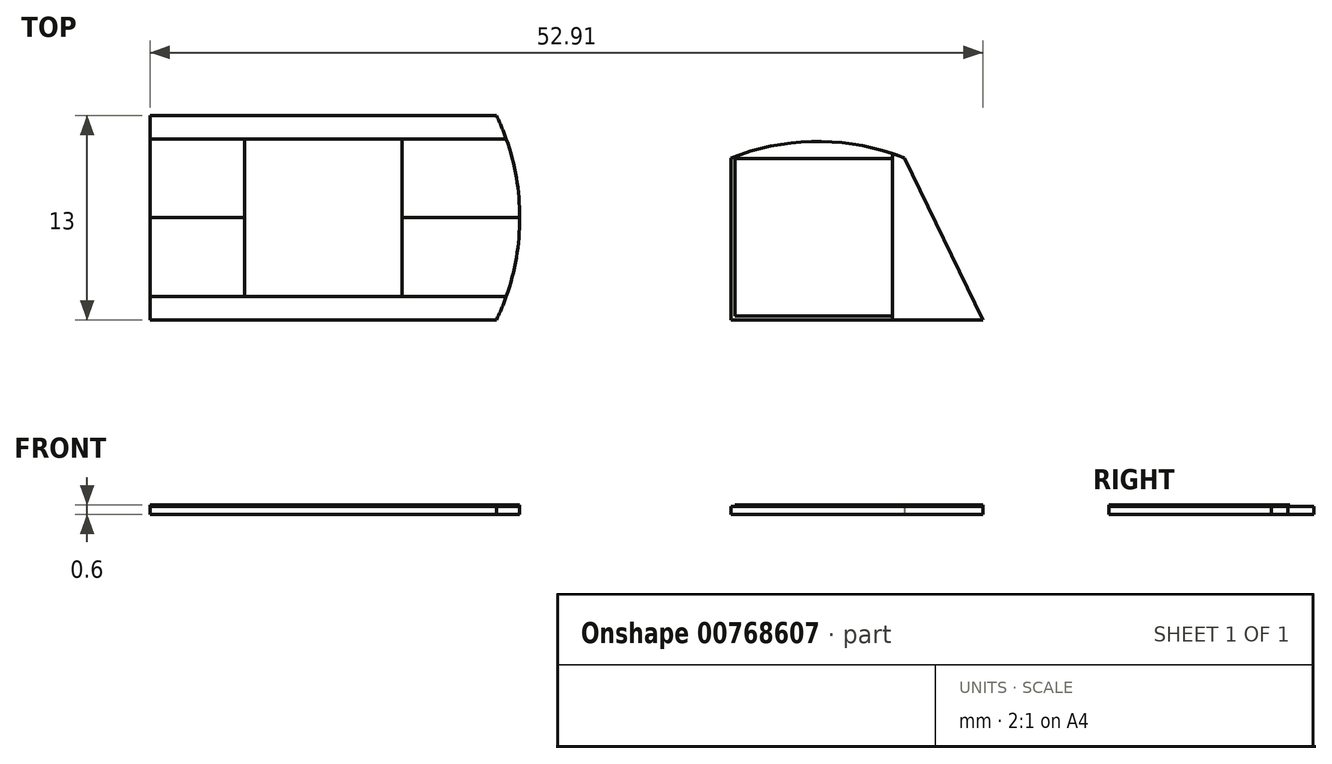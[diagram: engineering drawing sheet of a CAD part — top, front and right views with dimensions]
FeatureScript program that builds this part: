
annotation { "Feature Type Name" : "Feature", "Feature Type Description" : "" }
export const myFeature = defineFeature(function(context is Context, id is Id, definition is map)
    precondition{}
    {
        {
            var Q0;
            Q0=qCreatedBy(makeId("Top.planeOp"),FACE);
            var sketch = newSketch(context, id + "F0", { "sketchPlane" : qUnion([Q0])});
            skLineSegment(sketch, "E0.bottom", {"start": v(-26.15, 13) * mm, "end": v(-4.15, 13) * mm});
            skLineSegment(sketch, "E0.top", {"start": v(-26.15, 0) * mm, "end": v(-4.15, 0) * mm});
            skLineSegment(sketch, "E0.left", {"start": v(-26.15, 13) * mm, "end": v(-26.15, 0) * mm});
            skLineSegment(sketch, "E0.right", {"start": v(-4.15, 13) * mm, "end": v(-4.15, 0) * mm});
            skLineSegment(sketch, "E1.bottom", {"start": v(10.76, 10.3) * mm, "end": v(21.76, 10.3) * mm});
            skLineSegment(sketch, "E1.top", {"start": v(10.76, 0) * mm, "end": v(26.76, 0) * mm});
            skLineSegment(sketch, "E1.left", {"start": v(10.76, 10.3) * mm, "end": v(10.76, 0) * mm});
            skLineSegment(sketch, "E2", {"start": v(21.76, 10.3) * mm, "end": v(26.76, 0) * mm});
            skArc(sketch, "E3", {"start": v(-4.15, 0) * mm, "mid": v(-2.67, 6.5) * mm, "end": v(-4.15, 13) * mm});
            skArc(sketch, "E4", {"start": v(21.76, 10.3) * mm, "mid": v(16.26, 11.34) * mm, "end": v(10.76, 10.3) * mm});
            skSolve(sketch);
        }
        {
            var Q0;
            Q0=qSketchRegion(id+"F0",true);
            extrude(context, id + "F1", {"entities" : qUnion([Q0]), "depth" : 0.5 * mm, "offsetDistance" : 25 * mm});
        }
        {
            var Q0;
            Q0=makeQuery(id+"F1.opExtrude","CAP_FACE",FACE,{"disambiguationData":[OSD([sQuery(id+"F0.wireOp",EDGE,"E0.bottom"),sQuery(id+"F0.wireOp",EDGE,"E0.top"),sQuery(id+"F0.wireOp",EDGE,"E0.left"),sQuery(id+"F0.wireOp",EDGE,"E3")])],"isStart":false});
            var sketch = newSketch(context, id + "F2", { "sketchPlane" : qUnion([Q0])});
            skLineSegment(sketch, "E5", {"start": v(-26.15, 6.5) * mm, "end": v(-2.67, 6.5) * mm, "construction": true});
            skLineSegment(sketch, "E6.bottom", {"start": v(-10.15, 1.5) * mm, "end": v(-20.15, 1.5) * mm});
            skLineSegment(sketch, "E6.top", {"start": v(-10.15, 11.5) * mm, "end": v(-20.15, 11.5) * mm});
            skLineSegment(sketch, "E6.left", {"start": v(-10.15, 1.5) * mm, "end": v(-10.15, 11.5) * mm});
            skLineSegment(sketch, "E6.right", {"start": v(-20.15, 1.5) * mm, "end": v(-20.15, 11.5) * mm});
            skPoint(sketch, "E6.middle", {"position": v(-15.15, 6.5) * mm});
            skLineSegment(sketch, "E7.bottom", {"start": v(-20.15, 1.5) * mm, "end": v(-26.15, 1.5) * mm});
            skLineSegment(sketch, "E7.top", {"start": v(-20.15, 11.5) * mm, "end": v(-26.15, 11.5) * mm});
            skLineSegment(sketch, "E7.right", {"start": v(-26.15, 1.5) * mm, "end": v(-26.15, 11.5) * mm});
            skPoint(sketch, "E7.middle", {"position": v(-23.15, 6.5) * mm});
            skLineSegment(sketch, "E8.bottom", {"start": v(-10.15, 1.5) * mm, "end": v(-2.67, 1.5) * mm});
            skLineSegment(sketch, "E8.top", {"start": v(-10.15, 11.5) * mm, "end": v(-2.67, 11.5) * mm});
            skLineSegment(sketch, "E8.right", {"start": v(-2.67, 1.5) * mm, "end": v(-2.67, 11.5) * mm});
            skPoint(sketch, "E8.middle", {"position": v(-6.4, 6.5) * mm});
            skLineSegment(sketch, "E9", {"start": v(-20.15, 6.5) * mm, "end": v(-26.15, 6.5) * mm});
            skLineSegment(sketch, "E10", {"start": v(-10.15, 6.5) * mm, "end": v(-2.67, 6.5) * mm});
            skSolve(sketch);
        }
        {
            var Q0;
            Q0=makeQuery(id+"F1.opExtrude","CAP_FACE",FACE,{"disambiguationData":[OSD([sQuery(id+"F0.wireOp",EDGE,"E1.top"),sQuery(id+"F0.wireOp",EDGE,"E1.left"),sQuery(id+"F0.wireOp",EDGE,"E2"),sQuery(id+"F0.wireOp",EDGE,"E4")])],"isStart":false});
            var sketch = newSketch(context, id + "F3", { "sketchPlane" : qUnion([Q0])});
            skLineSegment(sketch, "E11.bottom", {"start": v(11, 0.25) * mm, "end": v(21, 0.25) * mm});
            skLineSegment(sketch, "E11.top", {"start": v(11, 10.25) * mm, "end": v(21, 10.25) * mm});
            skLineSegment(sketch, "E11.left", {"start": v(11, 0.25) * mm, "end": v(11, 10.25) * mm});
            skLineSegment(sketch, "E11.right", {"start": v(21, 0.25) * mm, "end": v(21, 10.25) * mm});
            skLineSegment(sketch, "E12", {"start": v(21, 10.25) * mm, "end": v(21, 10.57) * mm});
            skLineSegment(sketch, "E13", {"start": v(21, 0.25) * mm, "end": v(21, 0) * mm});
            skSolve(sketch);
        }
        {
            var Q0;
            {var subQ0=sQuery(id+"F2.wireOp",EDGE,"E7.bottom");Q0=makeQuery(id+"F2.imprint","IMPRINT",FACE,{"disambiguationData":[TD([[makeQuery(id+"F2.imprint","IMPRINT",EDGE,{"derivedFrom":subQ0}),-1.0]])]});}
            extrude(context, id + "F4", {"entities" : qUnion([Q0]), "depth" : 0.1 * mm, "offsetDistance" : 25 * mm});
        }
        {
            var Q0;
            {var subQ0=sQuery(id+"F2.wireOp",EDGE,"E7.top");Q0=makeQuery(id+"F2.imprint","IMPRINT",FACE,{"disambiguationData":[TD([[makeQuery(id+"F2.imprint","IMPRINT",EDGE,{"derivedFrom":subQ0}),1.0]])]});}
            extrude(context, id + "F5", {"entities" : qUnion([Q0]), "depth" : 0.1 * mm, "offsetDistance" : 25 * mm});
        }
        {
            var Q0;
            {var subQ1=sQuery(id+"F2.wireOp",EDGE,"E6.bottom");Q0=makeQuery(id+"F2.imprint","IMPRINT",FACE,{"disambiguationData":[TD([[makeQuery(id+"F2.imprint","IMPRINT",EDGE,{"derivedFrom":subQ1}),-1.0]])]});}
            extrude(context, id + "F6", {"entities" : qUnion([Q0]), "depth" : 0.1 * mm, "offsetDistance" : 25 * mm});
        }
        {
            var Q0;
            {var subQ5=sQuery(id+"F2.wireOp",EDGE,"E10");Q0=makeQuery(id+"F2.imprint","IMPRINT",FACE,{"disambiguationData":[TD([[makeQuery(id+"F2.imprint","IMPRINT",EDGE,{"derivedFrom":subQ5}),-1.0]])]});}
            extrude(context, id + "F7", {"entities" : qUnion([Q0]), "depth" : 0.1 * mm, "offsetDistance" : 25 * mm});
        }
        {
            var Q0;
            {var subQ5=sQuery(id+"F2.wireOp",EDGE,"E10");Q0=makeQuery(id+"F2.imprint","IMPRINT",FACE,{"disambiguationData":[TD([[makeQuery(id+"F2.imprint","IMPRINT",EDGE,{"derivedFrom":subQ5}),1.0]])]});}
            extrude(context, id + "F8", {"entities" : qUnion([Q0]), "depth" : 0.1 * mm, "offsetDistance" : 25 * mm});
        }
        {
            var Q0;
            Q0=makeQuery(id+"F3.imprint","IMPRINT",FACE,{"disambiguationData":[TD([[makeQuery(id+"F3.imprint","IMPRINT",EDGE,{"derivedFrom":sQuery(id+"F3.wireOp",EDGE,"E11.bottom")}),1.0]])]});
            extrude(context, id + "F9", {"entities" : qUnion([Q0]), "depth" : 0.1 * mm, "offsetDistance" : 25 * mm});
        }
        {
            var Q0;
            Q0=makeQuery(id+"F3.imprint","IMPRINT",FACE,{"disambiguationData":[TD([[makeQuery(id+"F3.imprint","IMPRINT",EDGE,{"derivedFrom":sQuery(id+"F3.wireOp",EDGE,"E11.right")}),-1.0]])]});
            extrude(context, id + "F10", {"entities" : qUnion([Q0]), "depth" : 0.1 * mm, "offsetDistance" : 25 * mm});
        }
    });
